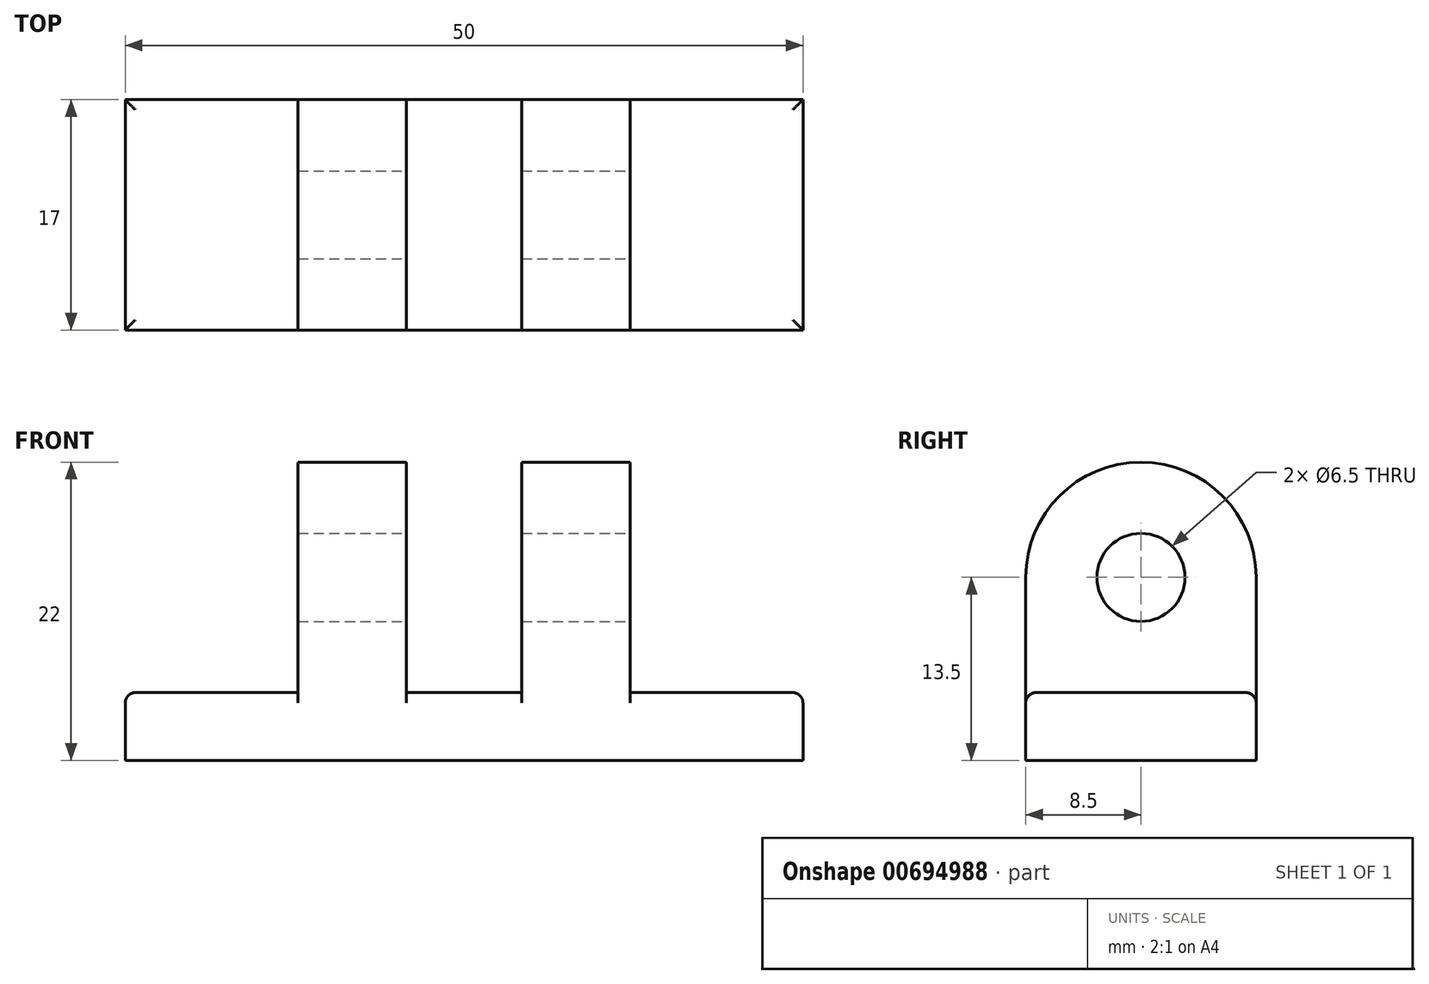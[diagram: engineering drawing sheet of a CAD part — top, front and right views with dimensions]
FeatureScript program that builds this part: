
annotation { "Feature Type Name" : "Feature", "Feature Type Description" : "" }
export const myFeature = defineFeature(function(context is Context, id is Id, definition is map)
    precondition{}
    {
        {
            var Q0;
            Q0=qCreatedBy(makeId("Top.planeOp"),FACE);
            var sketch = newSketch(context, id + "F0", { "sketchPlane" : qUnion([Q0])});
            skLineSegment(sketch, "E0.bottom", {"start": v(-25, 8.5) * mm, "end": v(25, 8.5) * mm});
            skLineSegment(sketch, "E0.top", {"start": v(-25, -8.5) * mm, "end": v(25, -8.5) * mm});
            skLineSegment(sketch, "E0.left", {"start": v(-25, 8.5) * mm, "end": v(-25, -8.5) * mm});
            skLineSegment(sketch, "E0.right", {"start": v(25, 8.5) * mm, "end": v(25, -8.5) * mm});
            skPoint(sketch, "E1", {"position": v(0, -8.5) * mm});
            skPoint(sketch, "E2", {"position": v(-25, 0) * mm});
            skSolve(sketch);
        }
        {
            var Q0;
            Q0=makeQuery(id+"F0.imprint","IMPRINT",FACE,{"disambiguationData":[TD([[makeQuery(id+"F0.imprint","IMPRINT",EDGE,{"derivedFrom":sQuery(id+"F0.wireOp",EDGE,"E0.bottom")}),-1.0]])]});
            extrude(context, id + "F1", {"entities" : qUnion([Q0]), "depth" : 5 * mm, "offsetDistance" : 25 * mm});
        }
        {
            var Q0;
            Q0=makeQuery(id+"F1.opExtrude","CAP_FACE",FACE,{"disambiguationData":[OSD([sQuery(id+"F0.wireOp",EDGE,"E0.bottom"),sQuery(id+"F0.wireOp",EDGE,"E0.top"),sQuery(id+"F0.wireOp",EDGE,"E0.left"),sQuery(id+"F0.wireOp",EDGE,"E0.right")])],"isStart":false});
            var sketch = newSketch(context, id + "F2", { "sketchPlane" : qUnion([Q0])});
            skLineSegment(sketch, "E3", {"start": v(-20.5, 8.5) * mm, "end": v(-20.5, -8.5) * mm, "construction": true});
            skLineSegment(sketch, "E4.MirrorCS", {"start": v(20.5, 8.5) * mm, "end": v(20.5, -8.5) * mm, "construction": true});
            skLineSegment(sketch, "E5", {"start": v(0, 8.5) * mm, "end": v(0, -8.5) * mm, "construction": true});
            skLineSegment(sketch, "E6", {"start": v(-4, 8.5) * mm, "end": v(-4, -8.5) * mm, "construction": true});
            skLineSegment(sketch, "E7.MirrorCS", {"start": v(4, 8.5) * mm, "end": v(4, -8.5) * mm, "construction": true});
            skLineSegment(sketch, "E8", {"start": v(-12.5, 8.5) * mm, "end": v(-12.5, -8.5) * mm, "construction": true});
            skLineSegment(sketch, "E9.MirrorCS", {"start": v(12.5, 8.5) * mm, "end": v(12.5, -8.5) * mm, "construction": true});
            skLineSegment(sketch, "E10", {"start": v(-4.25, 8.5) * mm, "end": v(-4.25, -8.5) * mm});
            skLineSegment(sketch, "E11", {"start": v(-12.25, 8.5) * mm, "end": v(-12.25, -8.5) * mm});
            skLineSegment(sketch, "E12.MirrorCS", {"start": v(4.25, 8.5) * mm, "end": v(4.25, -8.5) * mm});
            skLineSegment(sketch, "E13.MirrorCS", {"start": v(12.25, 8.5) * mm, "end": v(12.25, -8.5) * mm});
            skSolve(sketch);
        }
        {
            var Q0;
            Q0=sQuery(id+"F2.wireOp",EDGE,"E11");
            cPlane(context, id + "F3", {"entities" : qUnion([Q0]), "cplaneType" : CPlaneType.LINE_ANGLE, "offset" : 25 * mm, "angle" : 90 * degree, "width" : 150 * mm, "height" : 150 * mm});
        }
        {
            var Q0;
            Q0=qCreatedBy(id+"F3.planeOp",FACE);
            var sketch = newSketch(context, id + "F4", { "sketchPlane" : qUnion([Q0])});
            skCircle(sketch, "E14", {"center": v(0, 13.5) * mm, "radius": 8.5 * mm});
            skLineSegment(sketch, "E15", {"start": v(-8.5, 13.5) * mm, "end": v(-8.5, 5) * mm});
            skLineSegment(sketch, "E16.MirrorCS", {"start": v(8.5, 13.5) * mm, "end": v(8.5, 5) * mm});
            skLineSegment(sketch, "E17", {"start": v(-8.5, 5) * mm, "end": v(8.5, 5) * mm});
            skSolve(sketch);
        }
        {
            var Q0;
            Q0=qSketchRegion(id+"F4",true);
            extrude(context, id + "F5", {"entities" : qUnion([Q0]), "operationType" : NewBodyOperationType.ADD, "depth" : 8 * mm, "offsetDistance" : 25 * mm});
        }
        {
            var Q0;
            Q0=sQuery(id+"F2.wireOp",EDGE,"E12.MirrorCS");
            cPlane(context, id + "F6", {"entities" : qUnion([Q0]), "cplaneType" : CPlaneType.LINE_ANGLE, "offset" : 25 * mm, "angle" : 90 * degree, "width" : 150 * mm, "height" : 150 * mm});
        }
        {
            var Q0;
            Q0=qCreatedBy(id+"F6.planeOp",FACE);
            var sketch = newSketch(context, id + "F7", { "sketchPlane" : qUnion([Q0])});
            skCircle(sketch, "E18", {"center": v(0, 13.5) * mm, "radius": 8.5 * mm});
            skLineSegment(sketch, "E19", {"start": v(-8.5, 13.5) * mm, "end": v(-8.5, 5) * mm});
            skLineSegment(sketch, "E20.MirrorCS", {"start": v(8.5, 13.5) * mm, "end": v(8.5, 5) * mm});
            skLineSegment(sketch, "E21", {"start": v(-8.5, 5) * mm, "end": v(8.5, 5) * mm});
            skSolve(sketch);
        }
        {
            var Q0;
            Q0=qSketchRegion(id+"F7",true);
            extrude(context, id + "F8", {"entities" : qUnion([Q0]), "operationType" : NewBodyOperationType.ADD, "depth" : 8 * mm, "offsetDistance" : 25 * mm});
        }
        {
            var Q0;
            Q0=makeQuery(id+"F8.opExtrude","CAP_FACE",FACE,{"disambiguationData":[OSD([sQuery(id+"F7.wireOp",EDGE,"E18"),sQuery(id+"F7.wireOp",EDGE,"E19"),sQuery(id+"F7.wireOp",EDGE,"E20.MirrorCS"),sQuery(id+"F7.wireOp",EDGE,"E21")])],"isStart":false});
            var sketch = newSketch(context, id + "F9", { "sketchPlane" : qUnion([Q0])});
            skCircle(sketch, "E22", {"center": v(0, 13.5) * mm, "radius": 3.25 * mm});
            skSolve(sketch);
        }
        {
            var Q0;
            Q0=qSketchRegion(id+"F9",true);
            extrude(context, id + "F10", {"entities" : qUnion([Q0]), "operationType" : NewBodyOperationType.REMOVE, "oppositeDirection" : true, "depth" : 25 * mm, "offsetDistance" : 25 * mm});
        }
        {
            var Q0;
            {var subQ0=sQuery(id+"F0.wireOp",EDGE,"E0.right");var subQ1=sQuery(id+"F0.wireOp",EDGE,"E0.bottom");var subQ6=makeQuery(id+"F1.opExtrude","SWEPT_FACE",FACE,{"disambiguationData":[OSD([subQ0])]});Q0=makeQuery(id+"F8.boolean.opBoolean","SPLIT",EDGE,{"disambiguationData":[TD([subQ6])],"derivedFrom":makeQuery(id+"F5.boolean.opBoolean","SPLIT",EDGE,{"disambiguationData":[TD([subQ6])],"derivedFrom":makeQuery(id+"F1.opExtrude","CAP_EDGE",EDGE,{"disambiguationData":[OSD([subQ1])],"isStart":false})})});}
            var Q1;
            {var subQ0=sQuery(id+"F4.wireOp",EDGE,"E16.MirrorCS");var subQ1=makeQuery(id+"F5.opExtrude","CAP_FACE",FACE,{"disambiguationData":[OSD([sQuery(id+"F4.wireOp",EDGE,"E14"),sQuery(id+"F4.wireOp",EDGE,"E15"),subQ0,sQuery(id+"F4.wireOp",EDGE,"E17")])],"isStart":false});var subQ3=sQuery(id+"F0.wireOp",EDGE,"E0.right");var subQ4=sQuery(id+"F0.wireOp",EDGE,"E0.bottom");Q1=makeQuery(id+"F8.boolean.opBoolean","SPLIT",EDGE,{"disambiguationData":[TD([subQ1])],"derivedFrom":makeQuery(id+"F5.boolean.opBoolean","SPLIT",EDGE,{"disambiguationData":[TD([makeQuery(id+"F1.opExtrude","SWEPT_FACE",FACE,{"disambiguationData":[OSD([subQ3])]})])],"derivedFrom":makeQuery(id+"F1.opExtrude","CAP_EDGE",EDGE,{"disambiguationData":[OSD([subQ4])],"isStart":false})})});}
            var Q2;
            {var subQ0=sQuery(id+"F0.wireOp",EDGE,"E0.left");var subQ2=sQuery(id+"F0.wireOp",EDGE,"E0.bottom");Q2=makeQuery(id+"F5.boolean.opBoolean","SPLIT",EDGE,{"disambiguationData":[TD([makeQuery(id+"F1.opExtrude","SWEPT_FACE",FACE,{"disambiguationData":[OSD([subQ0])]})])],"derivedFrom":makeQuery(id+"F1.opExtrude","CAP_EDGE",EDGE,{"disambiguationData":[OSD([subQ2])],"isStart":false})});}
            var Q3;
            {var subQ0=sQuery(id+"F0.wireOp",EDGE,"E0.left");var subQ1=sQuery(id+"F0.wireOp",EDGE,"E0.top");Q3=makeQuery(id+"F5.boolean.opBoolean","SPLIT",EDGE,{"disambiguationData":[TD([makeQuery(id+"F1.opExtrude","SWEPT_FACE",FACE,{"disambiguationData":[OSD([subQ0])]})])],"derivedFrom":makeQuery(id+"F1.opExtrude","CAP_EDGE",EDGE,{"disambiguationData":[OSD([subQ1])],"isStart":false})});}
            var Q4;
            Q4=makeQuery(id+"F1.opExtrude","CAP_EDGE",EDGE,{"disambiguationData":[OSD([sQuery(id+"F0.wireOp",EDGE,"E0.left")])],"isStart":false});
            var Q5;
            {var subQ0=sQuery(id+"F4.wireOp",EDGE,"E15");var subQ2=makeQuery(id+"F5.opExtrude","CAP_FACE",FACE,{"disambiguationData":[OSD([sQuery(id+"F4.wireOp",EDGE,"E14"),subQ0,sQuery(id+"F4.wireOp",EDGE,"E16.MirrorCS"),sQuery(id+"F4.wireOp",EDGE,"E17")])],"isStart":false});var subQ3=sQuery(id+"F0.wireOp",EDGE,"E0.top");var subQ6=sQuery(id+"F0.wireOp",EDGE,"E0.right");Q5=makeQuery(id+"F8.boolean.opBoolean","SPLIT",EDGE,{"disambiguationData":[TD([subQ2])],"derivedFrom":makeQuery(id+"F5.boolean.opBoolean","SPLIT",EDGE,{"disambiguationData":[TD([makeQuery(id+"F1.opExtrude","SWEPT_FACE",FACE,{"disambiguationData":[OSD([subQ6])]})])],"derivedFrom":makeQuery(id+"F1.opExtrude","CAP_EDGE",EDGE,{"disambiguationData":[OSD([subQ3])],"isStart":false})})});}
            var Q6;
            {var subQ2=sQuery(id+"F0.wireOp",EDGE,"E0.right");var subQ3=makeQuery(id+"F1.opExtrude","SWEPT_FACE",FACE,{"disambiguationData":[OSD([subQ2])]});var subQ4=sQuery(id+"F0.wireOp",EDGE,"E0.top");Q6=makeQuery(id+"F8.boolean.opBoolean","SPLIT",EDGE,{"disambiguationData":[TD([subQ3])],"derivedFrom":makeQuery(id+"F5.boolean.opBoolean","SPLIT",EDGE,{"disambiguationData":[TD([subQ3])],"derivedFrom":makeQuery(id+"F1.opExtrude","CAP_EDGE",EDGE,{"disambiguationData":[OSD([subQ4])],"isStart":false})})});}
            var Q7;
            Q7=makeQuery(id+"F1.opExtrude","CAP_EDGE",EDGE,{"disambiguationData":[OSD([sQuery(id+"F0.wireOp",EDGE,"E0.right")])],"isStart":false});
            fillet(context, id + "F11", {"entities" : qUnion([Q0, Q1, Q2, Q3, Q4, Q5, Q6, Q7]), "radius" : .75 * mm, "tangentPropagation" : true, "allowEdgeOverflow" : false});
        }
    });
